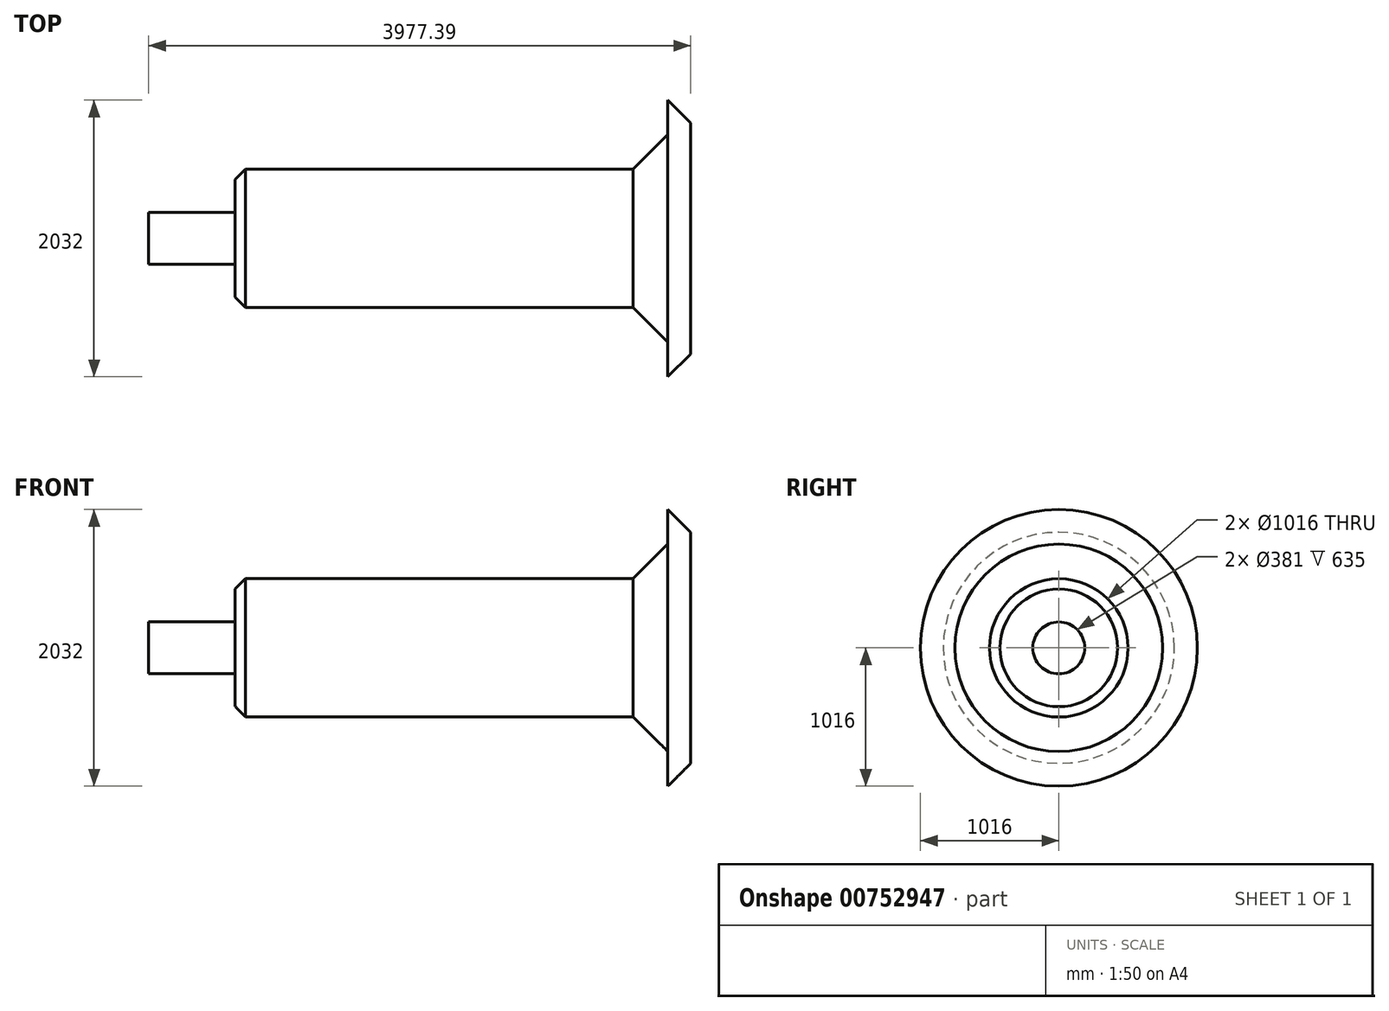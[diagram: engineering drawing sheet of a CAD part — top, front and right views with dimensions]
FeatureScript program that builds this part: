
annotation { "Feature Type Name" : "Feature", "Feature Type Description" : "" }
export const myFeature = defineFeature(function(context is Context, id is Id, definition is map)
    precondition{}
    {
        {
            var Q0;
            Q0=qCreatedBy(makeId("Front.planeOp"),FACE);
            var sketch = newSketch(context, id + "F0", { "sketchPlane" : qUnion([Q0])});
            skLineSegment(sketch, "E0", {"start": v(-1231.67, 0) * mm, "end": v(-1231.67, 190.5) * mm});
            skLineSegment(sketch, "E1", {"start": v(-1231.67, 190.5) * mm, "end": v(-596.67, 190.5) * mm});
            skLineSegment(sketch, "E2", {"start": v(-596.67, 190.5) * mm, "end": v(-596.67, 508) * mm});
            skLineSegment(sketch, "E3", {"start": v(-596.67, 508) * mm, "end": v(2324.33, 508) * mm});
            skLineSegment(sketch, "E4", {"start": v(-1231.67, 0) * mm, "end": v(3262.67, 0) * mm, "construction": true});
            skLineSegment(sketch, "E5", {"start": v(2324.33, 508) * mm, "end": v(2578.33, 762) * mm});
            skLineSegment(sketch, "E6", {"start": v(2578.33, 762) * mm, "end": v(2578.33, 1016) * mm});
            skLineSegment(sketch, "E7", {"start": v(2578.33, 1016) * mm, "end": v(2745.72, 848.6) * mm});
            skLineSegment(sketch, "E8", {"start": v(2745.72, 848.6) * mm, "end": v(2745.72, 0) * mm});
            skLineSegment(sketch, "E9", {"start": v(2324.33, 508) * mm, "end": v(2658.06, 508) * mm, "construction": true});
            skLineSegment(sketch, "E10", {"start": v(2745.72, 848.6) * mm, "end": v(2745.72, 1314.77) * mm, "construction": true});
            skSolve(sketch);
        }
        {
            var Q0;
            Q0=sQuery(id+"F0.wireOp",EDGE,"E8");
            var Q1;
            Q1=sQuery(id+"F0.wireOp",EDGE,"E6");
            var Q2;
            Q2=sQuery(id+"F0.wireOp",EDGE,"E5");
            var Q3;
            Q3=sQuery(id+"F0.wireOp",EDGE,"E7");
            var Q4;
            Q4=sQuery(id+"F0.wireOp",EDGE,"E0");
            var Q5;
            Q5=sQuery(id+"F0.wireOp",EDGE,"E1");
            var Q6;
            Q6=sQuery(id+"F0.wireOp",EDGE,"E3");
            var Q7;
            Q7=sQuery(id+"F0.wireOp",EDGE,"E2");
            var Q8;
            Q8=sQuery(id+"F0.wireOp",EDGE,"E4");
            revolve(context, id + "F1", {"bodyType" : ToolBodyType.SURFACE, "surfaceOperationType" : NewSurfaceOperationType.NEW, "surfaceEntities" : qUnion([Q0, Q1, Q2, Q3, Q4, Q5, Q6, Q7]), "axis" : qUnion([Q8]), "revolveType" : RevolveType.FULL});
        }
        {
            var Q0;
            Q0=makeQuery(id+"F1.opRevolve","SWEPT_EDGE",EDGE,{"disambiguationData":[OSD([sQuery(id+"F0.wireOp",VERTEX,"E2.end")])]});
            chamfer(context, id + "F2", {"entities" : qUnion([Q0]), "width" : 76.2 * mm, "tangentPropagation" : true});
        }
    });
